# Revit family: F1-Turnstile
name_source: partatom
category: Modele ogólne
units: mm (PartAtom-declared; Revit-internal decimal feet)

## family parameters
Może być obiektem nadrzędnym dla zbrojenia = Nie
Obiekt nadrzędny = Powierzchnia
Punkt obliczania pomieszczeń = Nie
Tnij formami wycięć po wczytaniu = Nie
Typ części = Normalny
Współdzielony = Nie
Wymiar okrągłego złącza = Użyj średnicy
Zachowaj orientację opisów = Nie

## types (1)
- F1-Turnstile
    Display Arrow Green = LED Green
    Display Arrow Red = LED Red
    Domyślna rzędna = 1219 mm
    Finish = Stainless Steel - Satin
    Height = 966 mm
    Lock = Stainless Steel - Polished
    Model = F1
    Opis = The device designed to assist pedestrian access control at guarded passage ways inside buildings. Possibility to equip with two types of  mechanisms: GA2 or ZA2.
    Producent = Gastop Production Sp. z o.o.
    Product website = https://www.gastopgroup.com
    Safty Instalation Margin = Tak
    Top Cover = Glass Cover
    URL = https://www.gastopgroup.com

## geometry (parser evidence)
native form markers: Sweep x11
no freeform markers — native parametric forms only
